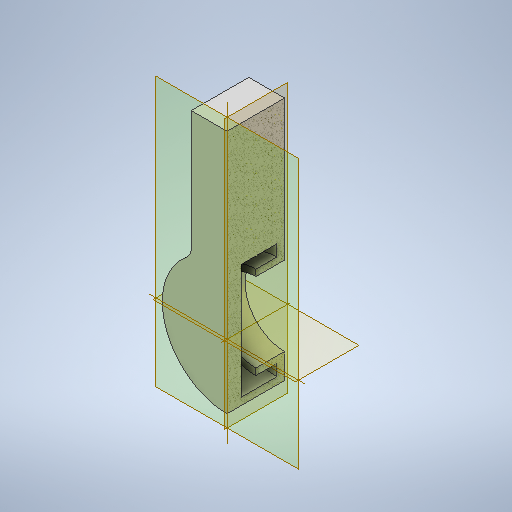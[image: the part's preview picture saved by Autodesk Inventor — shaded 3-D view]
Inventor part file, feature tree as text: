
AUTODESK INVENTOR PART (.ipt)
format: ipt  version: 2025.1 (Build 291241000, 241)  size: 313,344 bytes
history: native  units: mm
features: sketch x3, extrude x2, revolve x1
ambient origin geometry x8: Origin, YZ Plane, XZ Plane, XY Plane, X Axis, Y Axis, Z Axis, Center Point
bodies: Volumenkörper1 (feature_tree)
feature tree (6):
  extrude  "Extrusion1"  Depth=5.0mm
  extrude  "Extrusion2"  Depth=4.0mm
  revolve  "Umdrehung1"
  sketch  "Skizze1"  dims[d2=18.0mm d3=5.0mm]
  sketch  "Skizze3"  dims[d4=2.0mm d5=4.0mm]
  sketch  "Skizze5"  dims[d6=8.0mm d7=0.0mm d8=10.0mm d9=5.0mm d10=0.0mm d11=25.0mm d12=11.0mm d13=6.0mm d14=0.0mm d21=0.0mm d22=2.0mm d23=360.0deg d26=8.0mm d27=6.4mm]
